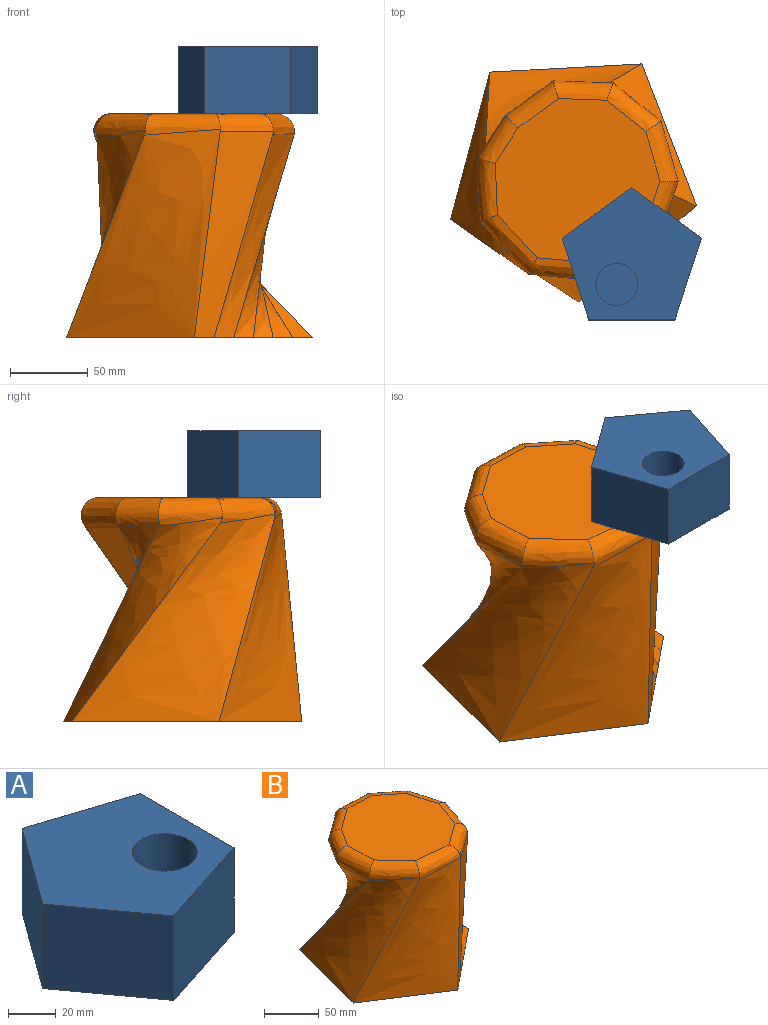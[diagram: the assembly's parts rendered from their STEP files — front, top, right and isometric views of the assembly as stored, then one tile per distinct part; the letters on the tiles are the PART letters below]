
ASSEMBLY  parts=2 mates=1
PART A: 9 faces, bbox 85.2x89.6x43.2 mm
  f0: plane 55.36x43.18mm, normal (1,0,0), area 2390.6mm2, adj f1,f4,f5,f6
  f1: plane 52.65x43.18mm, normal (0.31,0.95,0), area 2390.6mm2, adj f0,f2,f5,f6
  f2: plane 44.79x43.18mm, normal (-0.81,0.59,0), area 2390.6mm2, adj f1,f3,f5,f6
  f3: plane 44.79x43.18mm, normal (-0.81,-0.59,0), area 2390.6mm2, adj f2,f4,f5,f6
  f4: plane 52.65x43.18mm, normal (0.31,-0.95,0), area 2390.6mm2, adj f0,f3,f5,f6
  f5: plane 89.58x85.19mm, normal (0,0,1), area 4698.2mm2, adj f0,f1,f2,f3,f4,f7
  f6: plane 89.58x85.19mm, normal (0,0,-1), area 5273.3mm2, adj f0,f1,f2,f3,f4
  f7: cylinder r=13.53mm len=27.94mm, axis (0,0,1), area 2375.1mm2, adj f5,f8
  f8: plane 27.06x27.06mm, normal (0,0,1), area 575mm2, adj f7
PART B: 22 faces, bbox 158.2x159.6x144.2 mm
  f0: plane 158.25x153.15mm, normal (0,0,-1), area 16505.1mm2, adj f2,f3,f4,f5,f6,f7,f8,f9
  f1: plane 106.11x106.02mm, normal (0,0,1), area 8671.2mm2, adj f12,f13,f14,f15,f16,f17,f18,f19
  f2: bspline ~144.02x54.37mm, area 3919.2mm2, adj f0,f3,f11,f18,f20
  f3: bspline ~144.02x72.9mm, area 3770.7mm2, adj f0,f2,f4,f16,f18
  f4: bspline ~144.02x105.38mm, area 3464.1mm2, adj f0,f3,f5,f14,f16
  f5: bspline ~144.02x121.52mm, area 3070.6mm2, adj f0,f4,f6,f12,f14
  f6: bspline ~144.02x111.22mm, area 2723.2mm2, adj f0,f5,f7,f12,f13
  f7: bspline ~144.02x139.38mm, area 2639.1mm2, adj f0,f6,f8,f13,f15
  f8: bspline ~153.28x144.02mm, area 7579.9mm2, adj f0,f7,f9,f15,f17
  f9: bspline ~144.02x118.03mm, area 8184.1mm2, adj f0,f8,f10,f17,f19
  f10: bspline ~144.02x133.87mm, area 8879.8mm2, adj f0,f9,f11,f19,f21
  f11: bspline ~144.02x100.22mm, area 9516.4mm2, adj f0,f2,f10,f20,f21
  f12: bspline ~59.64x23.34mm, area 906.2mm2, adj f1,f5,f6,f13,f14
  f13: bspline ~56.6x51.03mm, area 955.5mm2, adj f1,f6,f7,f12,f15
  f14: bspline ~57x49.04mm, area 851.3mm2, adj f1,f4,f5,f12,f16
  f15: bspline ~53.49x37.18mm, area 775.1mm2, adj f1,f7,f8,f13,f17
  f16: bspline ~54.43x30.52mm, area 798.3mm2, adj f1,f3,f4,f14,f18
  f17: bspline ~50.42x27.1mm, area 837.6mm2, adj f1,f8,f9,f15,f19
  f18: bspline ~52.27x28.69mm, area 749.1mm2, adj f1,f2,f3,f16,f20
  f19: bspline ~53.39x49.29mm, area 855.8mm2, adj f1,f9,f10,f17,f21
  f20: bspline ~47.7x39.03mm, area 697.2mm2, adj f1,f2,f11,f18,f21
  f21: bspline ~60.81x16.52mm, area 822.9mm2, adj f1,f10,f11,f19,f20
PLACE A rot(axis=(0,0,-1),90deg) t=(-71.15,-47.08,188.8)mm
PLACE B t=(-110.01,9.93,44.79)mm fixed
MATE planar A.f6 <-> B.f1  axis (0,0,-1) through (-71.15,-47.08,188.8)mm
